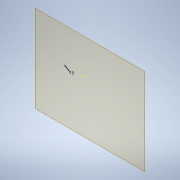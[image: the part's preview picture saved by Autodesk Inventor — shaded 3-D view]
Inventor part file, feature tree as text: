
AUTODESK INVENTOR PART (.ipt)
format: ipt  version: 2022 (Build 260153000, 153)  size: 94,720 bytes
history: native  units: mm
features: plane x1, extrude x1, sketch x1
ambient origin geometry x8: Origin, YZ Plane, XZ Plane, XY Plane, X Axis, Y Axis, Z Axis, Center Point
bodies: Solid1 (feature_tree)
feature tree (3):
  plane  "Work Plane1"
  extrude  "Extrusion1"  Depth=30.0mm TaperAngle=0.0deg
  sketch  "Sketch1"  dims[d0=7.62mm d1=30.0mm d2=0.0mm]
